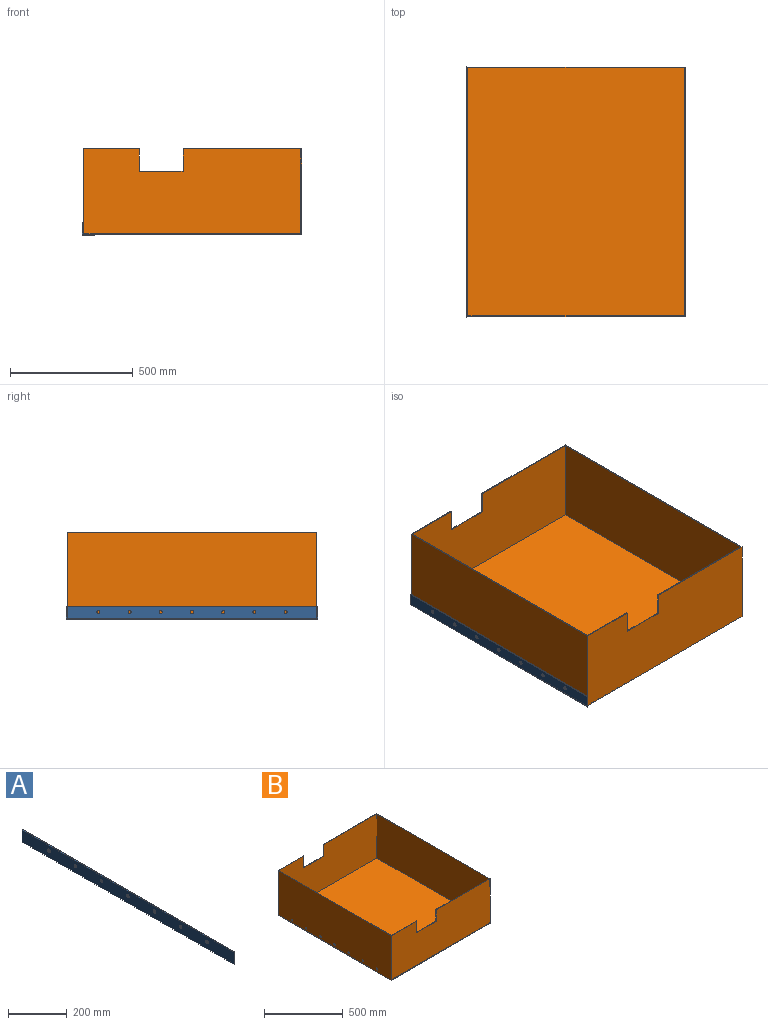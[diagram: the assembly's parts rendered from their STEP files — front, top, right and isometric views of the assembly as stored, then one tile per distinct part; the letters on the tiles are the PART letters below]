
ASSEMBLY  parts=2 mates=1
PART A: 21 faces, bbox 50.8x1022.4x50.8 mm
  f0: plane 1022.35x50.8mm, normal (-1,0,0), area 51048.6mm2, adj f1,f3,f6,f7,f8,f9,f10,f11
  f1: plane 1022.35x50.8mm, normal (0,0,-1), area 48594.7mm2, adj f0,f2,f6,f7,f15,f16,f17,f18
  f2: plane 920.75x3.18mm, normal (1,0,0), area 2923.4mm2, adj f1,f4,f6,f7
  f3: plane 1022.35x3.18mm, normal (0,0,1), area 3235.9mm2, adj f0,f5,f6,f7
  f4: plane 1016x47.63mm, normal (0,0,1), area 45358.8mm2, adj f2,f5,f6,f7,f15,f16,f17,f18
  f5: plane 1016x47.63mm, normal (1,0,0), area 47500.3mm2, adj f3,f4,f6,f7,f8,f9,f10,f11
  f6: plane 50.8x50.8mm, normal (0.71,0.71,0), area 441.9mm2, adj f0,f1,f2,f3,f4,f5
  f7: plane 50.8x50.8mm, normal (0.71,-0.71,0), area 441.9mm2, adj f0,f1,f2,f3,f4,f5
  f8: cylinder r=6.35mm len=12.7mm, axis (1,0,0), area 126.7mm2, adj f0,f5
  f9: cylinder r=6.35mm len=12.7mm, axis (1,0,0), area 126.7mm2, adj f0,f5
  f10: cylinder r=6.35mm len=12.7mm, axis (1,0,0), area 126.7mm2, adj f0,f5
  f11: cylinder r=6.35mm len=12.7mm, axis (1,0,0), area 126.7mm2, adj f0,f5
  f12: cylinder r=6.35mm len=12.7mm, axis (1,0,0), area 126.7mm2, adj f0,f5
  f13: cylinder r=6.35mm len=12.7mm, axis (1,0,0), area 126.7mm2, adj f0,f5
  f14: cylinder r=6.35mm len=12.7mm, axis (1,0,0), area 126.7mm2, adj f0,f5
  f15: cylinder r=6.35mm len=12.7mm, axis (0,0,1), area 126.7mm2, adj f1,f4
  f16: cylinder r=6.35mm len=12.7mm, axis (0,0,1), area 126.7mm2, adj f1,f4
  f17: cylinder r=6.35mm len=12.7mm, axis (0,0,1), area 126.7mm2, adj f1,f4
  f18: cylinder r=6.35mm len=12.7mm, axis (0,0,1), area 126.7mm2, adj f1,f4
  f19: cylinder r=6.35mm len=12.7mm, axis (0,0,1), area 126.7mm2, adj f1,f4
  f20: cylinder r=6.35mm len=12.7mm, axis (0,0,1), area 126.7mm2, adj f1,f4
PART B: 25 faces, bbox 889x1016x347.7 mm
  f0: plane 889x347.66mm, normal (0,-1,0), area 292983.3mm2, adj f1,f3,f4,f5,f10,f15,f16,f17
  f1: plane 1016x482.6mm, normal (0,0,1), area 6270.1mm2, adj f0,f2,f4,f6,f7,f9,f13,f16
  f2: plane 889x347.66mm, normal (0,1,0), area 292983.3mm2, adj f1,f3,f4,f5,f10,f12,f13,f14
  f3: plane 1016x347.66mm, normal (-1,0,0), area 352338.4mm2, adj f0,f2,f5,f10,f18,f19,f20,f21
  f4: plane 1016x347.66mm, normal (1,0,0), area 353225.1mm2, adj f0,f1,f2,f5
  f5: plane 1016x889mm, normal (0,0,-1), area 903224mm2, adj f0,f2,f3,f4
  f6: plane 1009.65x344.49mm, normal (-1,0,0), area 347811.8mm2, adj f1,f7,f9,f11
  f7: plane 882.65x344.49mm, normal (0,1,0), area 287973.2mm2, adj f1,f6,f8,f10,f11,f15,f16,f17
  f8: plane 1009.65x344.49mm, normal (1,0,0), area 346925.1mm2, adj f7,f9,f10,f11,f18,f19,f20,f21
  f9: plane 882.65x344.49mm, normal (0,-1,0), area 287973.2mm2, adj f1,f6,f8,f10,f11,f12,f13,f14
  f10: plane 1016x228.6mm, normal (0,0,1), area 4657.2mm2, adj f0,f2,f3,f7,f8,f9,f12,f17
  f11: plane 1009.65x882.65mm, normal (0,0,1), area 891167.6mm2, adj f6,f7,f8,f9
  f12: plane 90.49x3.18mm, normal (1,0,0), area 287.3mm2, adj f2,f9,f10,f14
  f13: plane 90.49x3.18mm, normal (-1,0,0), area 287.3mm2, adj f1,f2,f9,f14
  f14: plane 177.8x3.18mm, normal (0,0,1), area 564.5mm2, adj f2,f9,f12,f13
  f15: plane 177.8x3.18mm, normal (0,0,1), area 564.5mm2, adj f0,f7,f16,f17
  f16: plane 90.49x3.18mm, normal (-1,0,0), area 287.3mm2, adj f0,f1,f7,f15
  f17: plane 90.49x3.18mm, normal (1,0,0), area 287.3mm2, adj f0,f7,f10,f15
  f18: cylinder r=6.35mm len=12.7mm, axis (-1,0,0), area 126.7mm2, adj f3,f8
  f19: cylinder r=6.35mm len=12.7mm, axis (-1,0,0), area 126.7mm2, adj f3,f8
  f20: cylinder r=6.35mm len=12.7mm, axis (-1,0,0), area 126.7mm2, adj f3,f8
  f21: cylinder r=6.35mm len=12.7mm, axis (-1,0,0), area 126.7mm2, adj f3,f8
  f22: cylinder r=6.35mm len=12.7mm, axis (-1,0,0), area 126.7mm2, adj f3,f8
  f23: cylinder r=6.35mm len=12.7mm, axis (-1,0,0), area 126.7mm2, adj f3,f8
  f24: cylinder r=6.35mm len=12.7mm, axis (-1,0,0), area 126.7mm2, adj f3,f8
PLACE A t=(-314.23,463.74,-363.53)mm
PLACE B t=(133.44,-47.44,-360.55)mm
MATE fastened A.f14 <-> B.f18  axis (1,0,0) through (-311.06,-428.44,-335.15)mm
